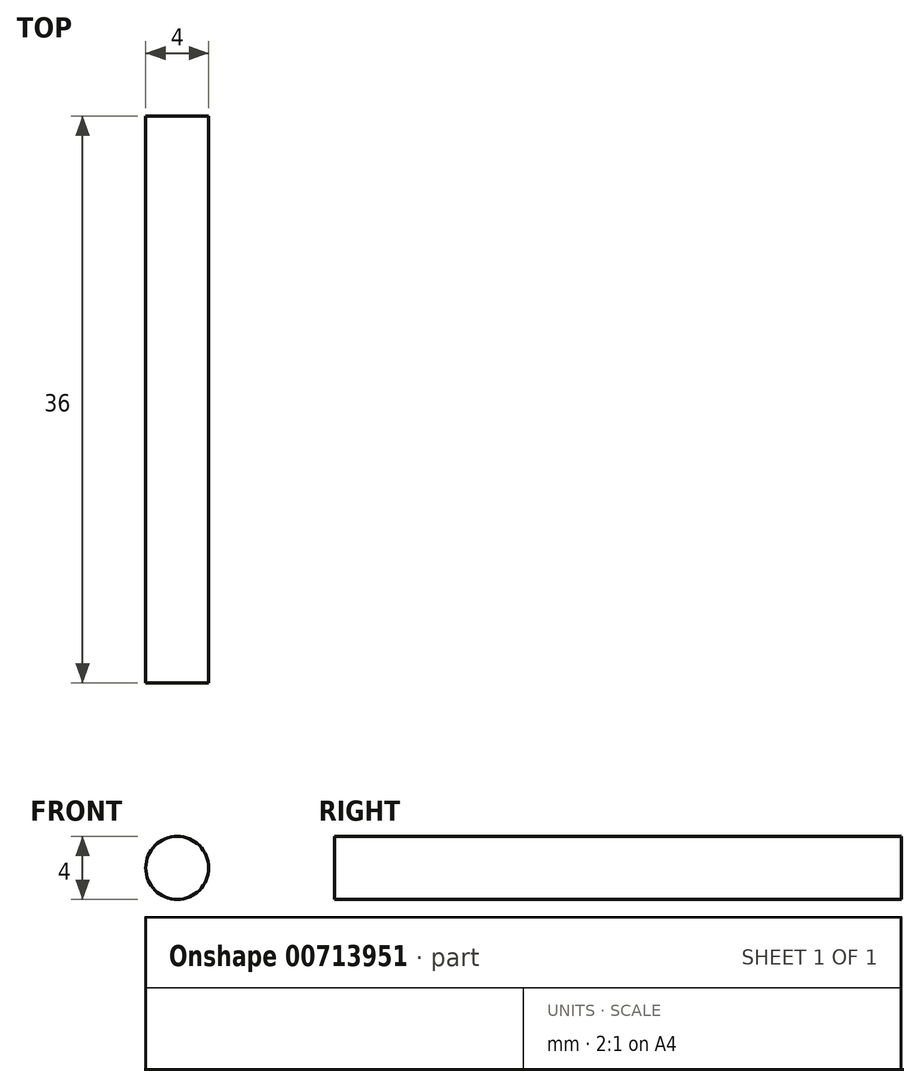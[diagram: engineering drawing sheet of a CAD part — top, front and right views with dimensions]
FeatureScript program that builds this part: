
annotation { "Feature Type Name" : "Feature", "Feature Type Description" : "" }
export const myFeature = defineFeature(function(context is Context, id is Id, definition is map)
    precondition{}
    {
        {
            var Q0;
            Q0=qCreatedBy(makeId("Front.planeOp"),FACE);
            var sketch = newSketch(context, id + "F0", { "sketchPlane" : qUnion([Q0])});
            skCircle(sketch, "E0", {"center": v(0, 0) * mm, "radius": 2 * mm});
            skSolve(sketch);
        }
        {
            var Q0;
            Q0=makeQuery(id+"F0.imprint","IMPRINT",FACE,{"disambiguationData":[TD([[makeQuery(id+"F0.imprint","IMPRINT",EDGE,{"derivedFrom":sQuery(id+"F0.wireOp",EDGE,"E0")}),1.0]])]});
            extrude(context, id + "F1", {"entities" : qUnion([Q0]), "depth" : 36 * mm, "offsetDistance" : 25 * mm});
        }
    });
